# Revit family: 306_82bbff842aca4f1c849c2f4f0a8b76
name_source: partatom
category: Pipe Accessories
units: mm (PartAtom-declared; Revit-internal decimal feet)

## family parameters
Always vertical = Yes
Cut with Voids When Loaded = No
Part Type = Valve - Breaks Into
Round Connector Dimension = Use Diameter
Shared = No
Work Plane-Based = No

## types (4) — shared parameters
AL1 = 72 mm
AL2 = 48 mm
AL3 = 90 mm
AL3__ve = -90 mm  [stored -0.295276 ft]
CC = 64 mm
CC1 = 38 mm
CC1__ve = -38 mm  [stored -0.124672 ft]
CenSd_RNR_6 = 6 mm  [stored 0.019685 ft]
Description = Chr.-plated 2-way zone valve, 230V actuator, M-M connections
G1 = 20 mm  [stored 0.0656168 ft]
G2 = 33 mm
GG = 36 mm
GG__ve = -36 mm  [stored -0.11811 ft]
KT = 10 mm  [stored 0.0328084 ft]
KT1 = 7 mm  [stored 0.0229659 ft]
KT2 = 3 mm  [stored 0.00984252 ft]
L2D = 144 mm
L2D_Min = 3048 mm
Manufacturer = FAR
QmdConnectorList = 301;D;302;D
RH = 4 mm  [stored 0.0131234 ft]
RNR = 7 mm  [stored 0.0229659 ft]
RW = 6 mm  [stored 0.019685 ft]
W2D = 25 mm  [stored 0.082021 ft]
magiPartTypeId = 306
magiProductFamilyId = 82bbff842aca4f1c849c2f4f0a8b76

## per-type parameters (varying)
- 300115 1: B0=28 mm; B1=4 mm  [stored 0.0131234 ft]; B2=10 mm  [stored 0.0328084 ft]; B22=8 mm  [stored 0.0262467 ft]; BR=12 mm  [stored 0.0393701 ft]; BR1=10 mm  [stored 0.0328084 ft]; CenSd_NR1_6=16 mm  [stored 0.0524934 ft]; CenSd_NRS1_6=6 mm  [stored 0.019685 ft]; CenSd_NR_6=19 mm  [stored 0.062336 ft]; D=25 mm; L1=7 mm  [stored 0.0229659 ft]; L1__ve=-7 mm; L2=72 mm; LR=41 mm; LR__ve=-41 mm; NR=22 mm  [stored 0.0721785 ft]; NR1=19 mm  [stored 0.062336 ft]; NR2=26 mm  [stored 0.0853018 ft]; NRS1=6 mm  [stored 0.019685 ft]; NT=14 mm  [stored 0.0459318 ft]; NT__ve=-14 mm  [stored -0.0459318 ft]; R=13 mm; RT=15 mm  [stored 0.0492126 ft]; RT1=18 mm  [stored 0.0590551 ft]; RT2=23 mm; TS=12 mm  [stored 0.0393701 ft]; TS__ve=-12 mm  [stored -0.0393701 ft]; magiProductId=1726f645174242c28cbff20ad7d764
- 300115 114: B0=33 mm; B1=5 mm  [stored 0.0164042 ft]; B2=10 mm  [stored 0.0328084 ft]; B22=8 mm  [stored 0.0262467 ft]; BR=15 mm  [stored 0.0492126 ft]; BR1=12 mm  [stored 0.0393701 ft]; CenSd_NR1_6=21 mm  [stored 0.0688976 ft]; CenSd_NRS1_6=7 mm  [stored 0.0229659 ft]; CenSd_NR_6=24 mm  [stored 0.0787402 ft]; D=32 mm; L1=8 mm  [stored 0.0262467 ft]; L1__ve=-8 mm; L2=82 mm; LR=49 mm; LR__ve=-49 mm; NR=28 mm; NR1=24 mm  [stored 0.0787402 ft]; NR2=31 mm  [stored 0.101706 ft]; NRS1=8 mm  [stored 0.0262467 ft]; NT=16 mm  [stored 0.0524934 ft]; NT__ve=-16 mm; R=16 mm  [stored 0.0524934 ft]; RT=19 mm  [stored 0.062336 ft]; RT1=23 mm; RT2=28 mm; TS=13 mm; TS__ve=-13 mm  [stored -0.0426509 ft]; magiProductId=f08519b185ec4c089e5141239e042f
- 300115 12: B0=18 mm  [stored 0.0590551 ft]; B1=3 mm  [stored 0.00984252 ft]; B2=12 mm  [stored 0.0393701 ft]; B22=10 mm  [stored 0.0328084 ft]; BR=7 mm  [stored 0.0229659 ft]; BR1=6 mm  [stored 0.019685 ft]; CenSd_NR1_6=10 mm  [stored 0.0328084 ft]; CenSd_NRS1_6=3 mm  [stored 0.00984252 ft]; CenSd_NR_6=11 mm; D=15 mm; L1=6 mm  [stored 0.019685 ft]; L1__ve=-6 mm  [stored -0.019685 ft]; L2=55 mm; LR=25 mm  [stored 0.082021 ft]; LR__ve=-25 mm; NR=13 mm; NR1=11 mm; NR2=16 mm  [stored 0.0524934 ft]; NRS1=4 mm  [stored 0.0131234 ft]; NT=11 mm; NT__ve=-11 mm; R=8 mm  [stored 0.0262467 ft]; RT=9 mm  [stored 0.0295276 ft]; RT1=11 mm; RT2=14 mm  [stored 0.0459318 ft]; TS=13 mm; TS__ve=-13 mm  [stored -0.0426509 ft]; magiProductId=e5f44b288bd44e73a8be78a9bcda85
- 300115 34: B0=23 mm; B1=4 mm  [stored 0.0131234 ft]; B2=12 mm  [stored 0.0393701 ft]; B22=10 mm  [stored 0.0328084 ft]; BR=10 mm  [stored 0.0328084 ft]; BR1=8 mm  [stored 0.0262467 ft]; CenSd_NR1_6=13 mm; CenSd_NRS1_6=4 mm  [stored 0.0131234 ft]; CenSd_NR_6=15 mm  [stored 0.0492126 ft]; D=20 mm; L1=6 mm  [stored 0.019685 ft]; L1__ve=-6 mm  [stored -0.019685 ft]; L2=62 mm; LR=31 mm  [stored 0.101706 ft]; LR__ve=-31 mm; NR=18 mm  [stored 0.0590551 ft]; NR1=15 mm  [stored 0.0492126 ft]; NR2=21 mm  [stored 0.0688976 ft]; NRS1=5 mm  [stored 0.0164042 ft]; NT=12 mm  [stored 0.0393701 ft]; NT__ve=-12 mm  [stored -0.0393701 ft]; R=10 mm  [stored 0.0328084 ft]; RT=12 mm  [stored 0.0393701 ft]; RT1=14 mm  [stored 0.0459318 ft]; RT2=19 mm  [stored 0.062336 ft]; TS=13 mm; TS__ve=-13 mm  [stored -0.0426509 ft]; magiProductId=0273a7fd17934a97878f65b45ca933

note: column(s) folded — value = type name in every type: MC Product Code

note: [stored X ft] marks values corroborated as IEEE doubles in the binary element streams (Revit-internal decimal feet)

## geometry (parser evidence)
native form markers: Sweep x3
no freeform markers — native parametric forms only
